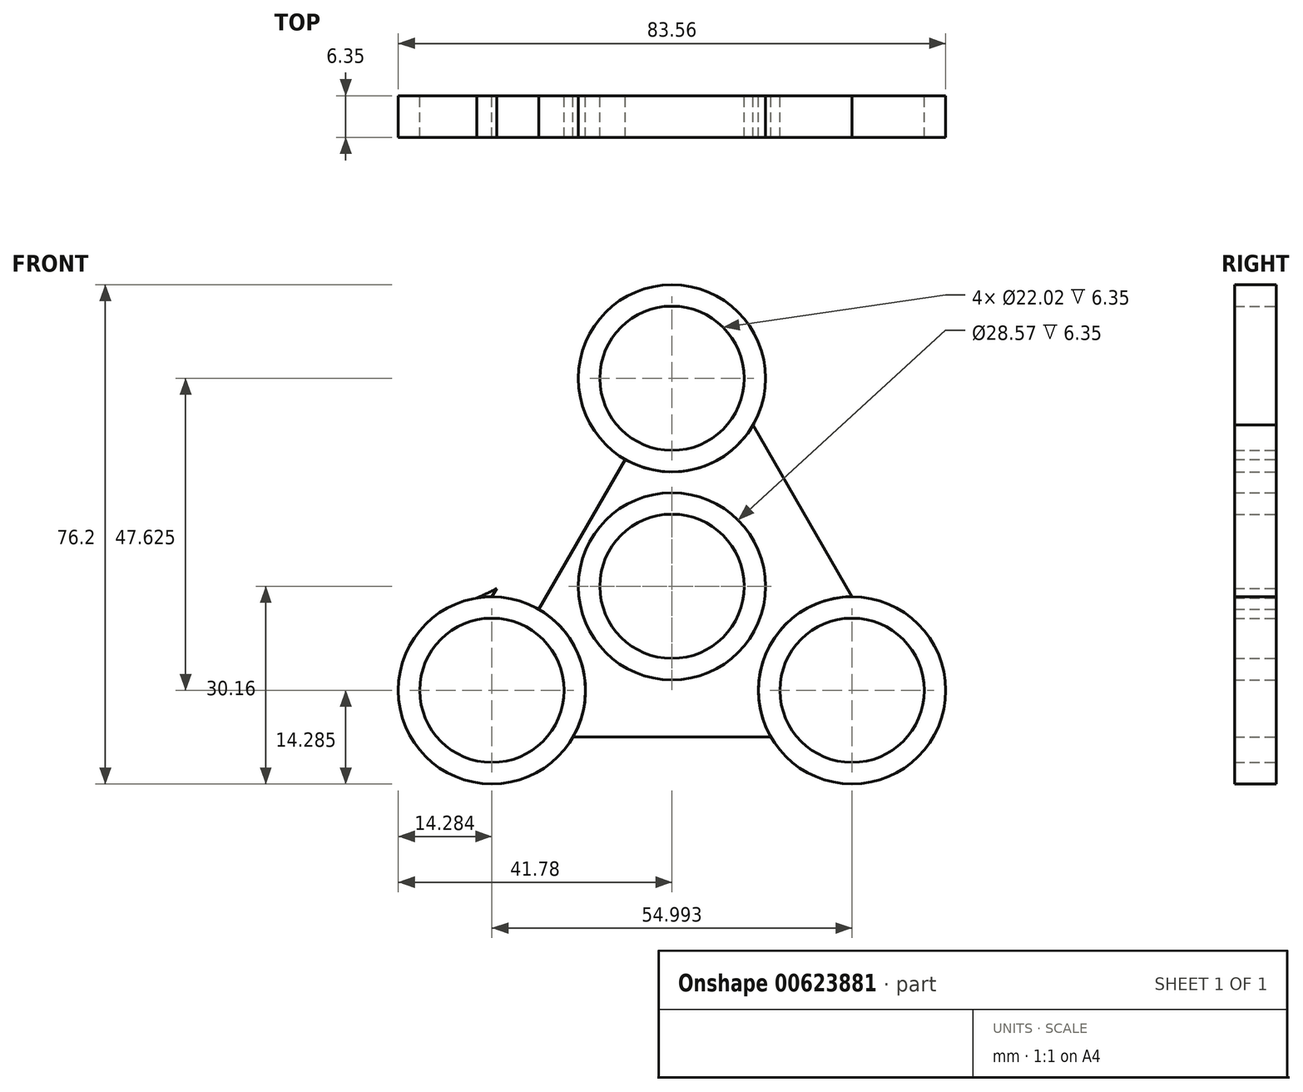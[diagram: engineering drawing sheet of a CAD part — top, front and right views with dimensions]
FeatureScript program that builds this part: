
annotation { "Feature Type Name" : "Feature", "Feature Type Description" : "" }
export const myFeature = defineFeature(function(context is Context, id is Id, definition is map)
    precondition{}
    {
        {
            var Q0;
            Q0=qCreatedBy(makeId("Front.planeOp"),FACE);
            var sketch = newSketch(context, id + "F0", { "sketchPlane" : qUnion([Q0])});
            skCircle(sketch, "E0", {"center": v(0, 0) * mm, "radius": 11.01 * mm});
            skCircle(sketch, "E1", {"center": v(0, 0) * mm, "radius": 14.29 * mm});
            skCircle(sketch, "E2", {"center": v(0, 31.75) * mm, "radius": 11.01 * mm});
            skCircle(sketch, "E3", {"center": v(0, 31.75) * mm, "radius": 14.29 * mm});
            skCircle(sketch, "E4.1.0", {"center": v(-27.5, -15.87) * mm, "radius": 14.29 * mm});
            skCircle(sketch, "E4.1.1", {"center": v(-27.5, -15.87) * mm, "radius": 11.01 * mm});
            skCircle(sketch, "E4.2.0", {"center": v(27.5, -15.88) * mm, "radius": 14.29 * mm});
            skCircle(sketch, "E4.2.1", {"center": v(27.5, -15.88) * mm, "radius": 11.01 * mm});
            skSolve(sketch);
        }
        {
            var Q0;
            Q0=makeQuery(id+"F0.imprint","IMPRINT",FACE,{"disambiguationData":[TD([[makeQuery(id+"F0.imprint","IMPRINT",EDGE,{"derivedFrom":sQuery(id+"F0.wireOp",EDGE,"E2")}),-1.0]])]});
            var Q1;
            Q1=makeQuery(id+"F0.imprint","IMPRINT",FACE,{"disambiguationData":[TD([[makeQuery(id+"F0.imprint","IMPRINT",EDGE,{"derivedFrom":sQuery(id+"F0.wireOp",EDGE,"E0")}),-1.0]])]});
            var Q2;
            Q2=makeQuery(id+"F0.imprint","IMPRINT",FACE,{"disambiguationData":[TD([[makeQuery(id+"F0.imprint","IMPRINT",EDGE,{"derivedFrom":sQuery(id+"F0.wireOp",EDGE,"E4.2.0")}),1.0]])]});
            var Q3;
            Q3=makeQuery(id+"F0.imprint","IMPRINT",FACE,{"disambiguationData":[TD([[makeQuery(id+"F0.imprint","IMPRINT",EDGE,{"derivedFrom":sQuery(id+"F0.wireOp",EDGE,"E4.1.0")}),1.0]])]});
            extrude(context, id + "F1", {"entities" : qUnion([Q0, Q1, Q2, Q3]), "depth" : 6.35 * mm, "offsetDistance" : 25.4 * mm});
        }
        {
            var Q0;
            Q0=qCreatedBy(makeId("Front.planeOp"),FACE);
            var sketch = newSketch(context, id + "F2", { "sketchPlane" : qUnion([Q0])});
            skArc(sketch, "E5", {"start": v(-30.18, -1.93) * mm, "mid": v(-17.09, 9.04) * mm, "end": v(-13.31, 25.71) * mm});
            skArc(sketch, "E6", {"start": v(13.11, 25.71) * mm, "mid": v(17.85, 8.87) * mm, "end": v(31.6, -1.93) * mm});
            skArc(sketch, "E7", {"start": v(16.77, -25.5) * mm, "mid": v(-0.14, -18.6) * mm, "end": v(-16.97, -25.71) * mm});
            skCircle(sketch, "E8", {"center": v(0, 0) * mm, "radius": 11.01 * mm});
            skCircle(sketch, "E9", {"center": v(0, 31.75) * mm, "radius": 11.01 * mm});
            skCircle(sketch, "E10.1.0", {"center": v(-27.5, -15.87) * mm, "radius": 11.01 * mm});
            skCircle(sketch, "E10.2.0", {"center": v(27.5, -15.88) * mm, "radius": 11.01 * mm});
            skLineSegment(sketch, "E11", {"start": v(0, 0) * mm, "end": v(-27.5, -15.87) * mm});
            skLineSegment(sketch, "E12", {"start": v(27.5, -15.88) * mm, "end": v(-27.5, -15.87) * mm});
            skLineSegment(sketch, "E13", {"start": v(27.5, -15.88) * mm, "end": v(0, 0) * mm});
            skLineSegment(sketch, "E14", {"start": v(0, 31.75) * mm, "end": v(-27.5, -15.87) * mm});
            skLineSegment(sketch, "E15", {"start": v(0, 0) * mm, "end": v(0, 31.75) * mm});
            skLineSegment(sketch, "E16", {"start": v(27.5, -15.88) * mm, "end": v(0, 31.75) * mm});
            skLineSegment(sketch, "E17", {"start": v(0, 31.75) * mm, "end": v(0, 46.04) * mm});
            skLineSegment(sketch, "E18.1.0", {"start": v(-27.5, -15.87) * mm, "end": v(-39.87, -23.02) * mm});
            skLineSegment(sketch, "E18.2.0", {"start": v(27.5, -15.88) * mm, "end": v(39.87, -23.02) * mm});
            skLineSegment(sketch, "E19", {"start": v(-39.87, -23.02) * mm, "end": v(0, 46.04) * mm});
            skLineSegment(sketch, "E20", {"start": v(0, 46.04) * mm, "end": v(39.87, -23.02) * mm});
            skLineSegment(sketch, "E21", {"start": v(-39.87, -23.02) * mm, "end": v(39.87, -23.02) * mm});
            skCircle(sketch, "E22", {"center": v(0, 31.75) * mm, "radius": 14.29 * mm});
            skCircle(sketch, "E23.1.0", {"center": v(-27.5, -15.87) * mm, "radius": 14.29 * mm});
            skCircle(sketch, "E23.2.0", {"center": v(27.5, -15.88) * mm, "radius": 14.29 * mm});
            skCircle(sketch, "E24", {"center": v(0, 0) * mm, "radius": 14.29 * mm});
            skSolve(sketch);
        }
        {
            var Q0;
            {var subQ0=sQuery(id+"F2.wireOp",EDGE,"E19");var subQ1=sQuery(id+"F2.wireOp",EDGE,"E5");var subQ2=makeQuery(id+"F2.imprint","INTERSECT",VERTEX,{"disambiguationData":[OD(0.0)],"derivedFrom":[subQ1,subQ0]});Q0=makeQuery(id+"F2.imprint","IMPRINT",FACE,{"disambiguationData":[TD([[makeQuery(id+"F2.imprint","IMPRINT",EDGE,{"disambiguationData":[TD([[subQ2,1.0]])],"derivedFrom":subQ1}),-1.0]])]});}
            var Q1;
            {var subQ0=sQuery(id+"F2.wireOp",EDGE,"E19");var subQ1=sQuery(id+"F2.wireOp",EDGE,"E5");var subQ2=makeQuery(id+"F2.imprint","INTERSECT",VERTEX,{"disambiguationData":[OD(0.0)],"derivedFrom":[subQ1,subQ0]});Q1=makeQuery(id+"F2.imprint","IMPRINT",FACE,{"disambiguationData":[TD([[makeQuery(id+"F2.imprint","IMPRINT",EDGE,{"disambiguationData":[TD([[subQ2,1.0]])],"derivedFrom":subQ1}),1.0]])]});}
            var Q2;
            {var subQ5=sQuery(id+"F2.wireOp",EDGE,"E24");var subQ9=sQuery(id+"F2.wireOp",EDGE,"E11");var subQ11=makeQuery(id+"F2.imprint","INTERSECT",VERTEX,{"derivedFrom":[subQ9,subQ5]});Q2=makeQuery(id+"F2.imprint","IMPRINT",FACE,{"disambiguationData":[TD([[makeQuery(id+"F2.imprint","IMPRINT",EDGE,{"disambiguationData":[TD([[subQ11,-1.0]])],"derivedFrom":subQ9}),-1.0]])]});}
            var Q3;
            {var subQ1=sQuery(id+"F2.wireOp",EDGE,"E11");var subQ8=sQuery(id+"F2.wireOp",EDGE,"E24");var subQ11=makeQuery(id+"F2.imprint","INTERSECT",VERTEX,{"derivedFrom":[subQ1,subQ8]});Q3=makeQuery(id+"F2.imprint","IMPRINT",FACE,{"disambiguationData":[TD([[makeQuery(id+"F2.imprint","IMPRINT",EDGE,{"disambiguationData":[TD([[subQ11,-1.0]])],"derivedFrom":subQ1}),1.0]])]});}
            var Q4;
            {var subQ0=sQuery(id+"F2.wireOp",EDGE,"E21");var subQ1=sQuery(id+"F2.wireOp",EDGE,"E7");var subQ2=makeQuery(id+"F2.imprint","INTERSECT",VERTEX,{"disambiguationData":[OD(0.0)],"derivedFrom":[subQ1,subQ0]});Q4=makeQuery(id+"F2.imprint","IMPRINT",FACE,{"disambiguationData":[TD([[makeQuery(id+"F2.imprint","IMPRINT",EDGE,{"disambiguationData":[TD([[subQ2,1.0]])],"derivedFrom":subQ1}),1.0]])]});}
            var Q5;
            {var subQ0=sQuery(id+"F2.wireOp",EDGE,"E21");var subQ1=sQuery(id+"F2.wireOp",EDGE,"E7");var subQ9=makeQuery(id+"F2.imprint","INTERSECT",VERTEX,{"disambiguationData":[OD(0.0)],"derivedFrom":[subQ1,subQ0]});Q5=makeQuery(id+"F2.imprint","IMPRINT",FACE,{"disambiguationData":[TD([[makeQuery(id+"F2.imprint","IMPRINT",EDGE,{"disambiguationData":[TD([[subQ9,1.0]])],"derivedFrom":subQ1}),-1.0]])]});}
            var Q6;
            {var subQ7=sQuery(id+"F2.wireOp",EDGE,"E23.2.0");var subQ9=sQuery(id+"F2.wireOp",EDGE,"E13");var subQ10=makeQuery(id+"F2.imprint","INTERSECT",VERTEX,{"derivedFrom":[subQ9,subQ7]});Q6=makeQuery(id+"F2.imprint","IMPRINT",FACE,{"disambiguationData":[TD([[makeQuery(id+"F2.imprint","IMPRINT",EDGE,{"disambiguationData":[TD([[subQ10,-1.0]])],"derivedFrom":subQ9}),-1.0]])]});}
            var Q7;
            {var subQ0=sQuery(id+"F2.wireOp",EDGE,"E20");var subQ1=sQuery(id+"F2.wireOp",EDGE,"E6");var subQ5=makeQuery(id+"F2.imprint","INTERSECT",VERTEX,{"disambiguationData":[OD(0.0)],"derivedFrom":[subQ1,subQ0]});Q7=makeQuery(id+"F2.imprint","IMPRINT",FACE,{"disambiguationData":[TD([[makeQuery(id+"F2.imprint","IMPRINT",EDGE,{"disambiguationData":[TD([[subQ5,-1.0]])],"derivedFrom":subQ1}),-1.0]])]});}
            var Q8;
            {var subQ0=sQuery(id+"F2.wireOp",EDGE,"E20");var subQ1=sQuery(id+"F2.wireOp",EDGE,"E6");var subQ2=makeQuery(id+"F2.imprint","INTERSECT",VERTEX,{"disambiguationData":[OD(0.0)],"derivedFrom":[subQ1,subQ0]});Q8=makeQuery(id+"F2.imprint","IMPRINT",FACE,{"disambiguationData":[TD([[makeQuery(id+"F2.imprint","IMPRINT",EDGE,{"disambiguationData":[TD([[subQ2,-1.0]])],"derivedFrom":subQ1}),1.0]])]});}
            extrude(context, id + "F3", {"entities" : qUnion([Q0, Q1, Q2, Q3, Q4, Q5, Q6, Q7, Q8]), "depth" : 6.35 * mm, "offsetDistance" : 25.4 * mm});
        }
    });
